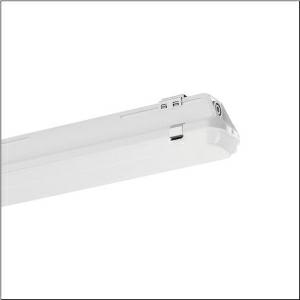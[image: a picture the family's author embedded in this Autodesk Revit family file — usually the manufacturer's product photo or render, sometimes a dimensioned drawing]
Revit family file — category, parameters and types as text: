
# Revit family: monsun_r__12_51fp11mp4b0q_bed7
name_source: partatom
category: Lighting Fixtures
units: mm (PartAtom-declared; Revit-internal decimal feet)

## family parameters
Cut with Voids When Loaded = No
Host = Face
Light Source = No
Part Type = Normal
Room Calculation Point = No
Round Connector Dimension = Use Diameter
Shared = No

## types (1)
- --- (1 x LED, 11900 lm, 66.2 W, 4000K)
    Apparent Load = 66 VA
    CIE Flux Codes = 71 88 97 97 100
    Color Rendering = 80
    Color Temperature = 4000K
    Default Elevation = 1800 mm
    Description = Monsun® 12, damp-proof luminaire, chain hanger, primary optical cover: enclosure, of PMMA, light emission: direct distribution, primary light characteristic: symmetric, installation type: suspended mounting, surface-mounted, horizontal mounting, vertical mounting, LED rated luminous flux: 11.900 lm, light colour: 840, colour temperature: 4000K, control gear: ECG, with terminal, 3-pole, max. 2.5mm², mains connection: 220..240V, AC, 50/60Hz, rated input power: 66W, luminaire housing, of glass-fibre reinforced polyester, uncoated, bright grey, length: 1.590 mm, width: 90 mm, height: 88mm, clip for enclosure, of stainless steel (V2A), ceiling mounting element, of stainless steel (V2A), chain hanger, of stainless steel (V2A), protection rating (complete): IP66, insulation class (complete): insulation class I (protective earthing), certification: CE, ENEC, VDE, protection symbol: D, impact resistance: IK04, permissible ambient temperature for indoor applications: -35..+35°C, standard: EN 50419, EN 60598-2-1, no direct snow, no direct sun, no direct rain, for indoor or canopied outdoor use, corresponds to IFS (International Featured Standards) requirements for safety and quality in the food industry, for animal farming (ammonia tested): for use in cowhouse, pig house, horse-stables... (not for use in poultry stables), AT max for animal farming = 40°C, packaging unit: 1 piece
    Height = 89 mm
    Lamp = 1 x LED
    Lamp Light Flux = 11900 lm
    Lamp Power = 66.2 W
    Lamp count = 1
    Length = 1590 mm
    Luminous efficacy = 180 lm/W
    Manufacturer = Siteco
    ModVariant = No
    Model = 51FP11MP4B0Q
    Mounting Place = Ceiling
    Mounting Type = Pendant
    Number of Poles = 1
    OnlyDefault = Yes
    Power Factor = 1
    Product Name = Monsun® 12
    Product group = damp-proof luminaire | ceiling pendant
    ProductGroupID = 908
    Protection Class = Protection class I
    Protection Degree = IP 66
    RLX_Detail_Level = 1
    RlxData = <blob elided: 89849 chars, md5=1cf0744e>
    Socket = socket
    Standby Power = 0 W
    System Light Flux = 11900 lm
    System Power = 66 W
    Type Comments = factory setting: luminous flux: 100 % | (A | C | E) | 155 mA
    Type Image = l_1004748.jpg
    URL = http://relux.com
    VarID = @adj_136005
    Voltage = 0 V
    Weight = 0.00 kg
    Width = 90 mm

## geometry (parser evidence)
native form markers: Blend x4, Sweep x10
no freeform markers — native parametric forms only
